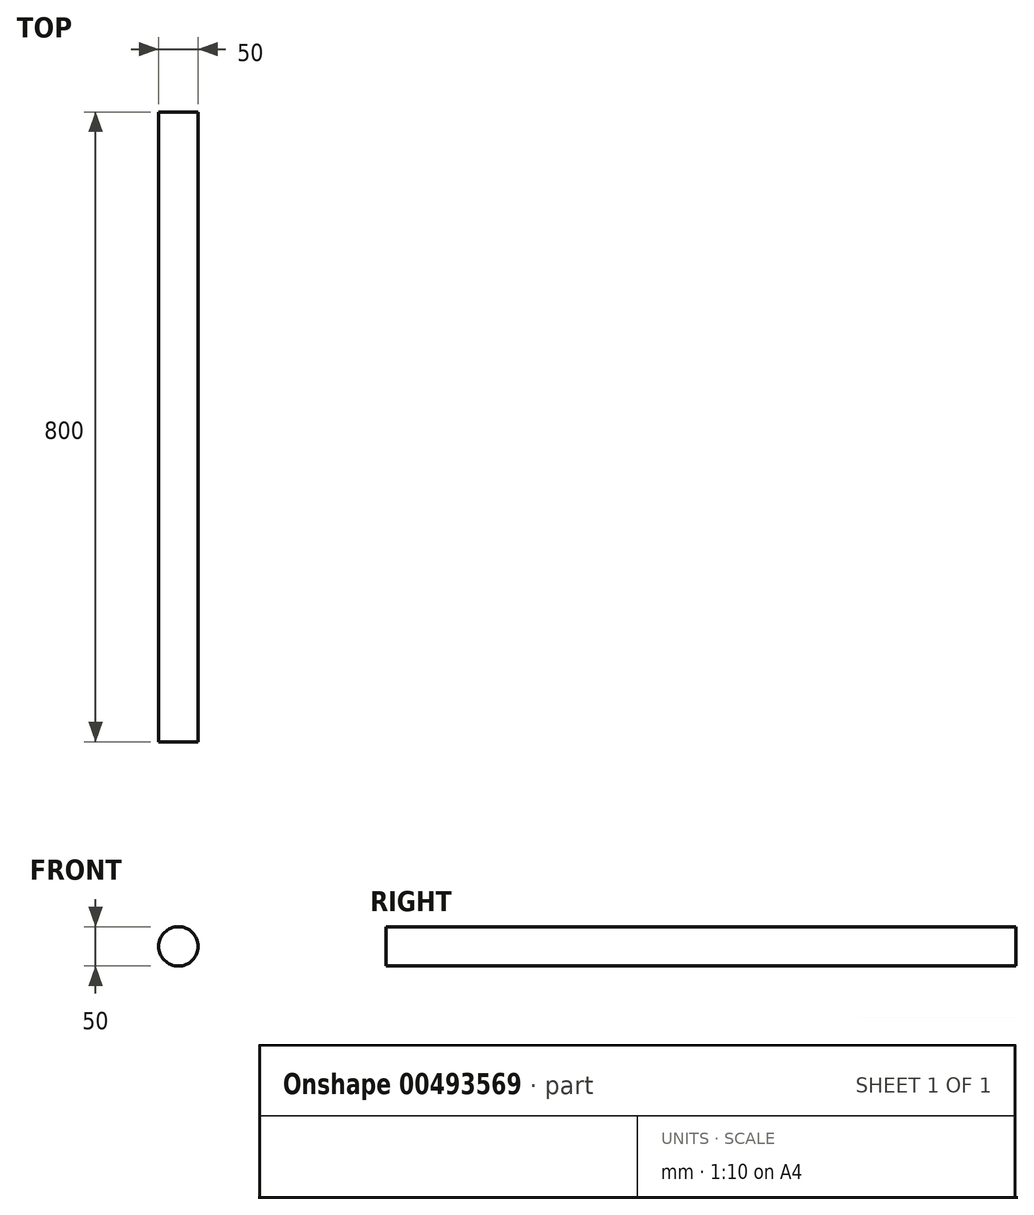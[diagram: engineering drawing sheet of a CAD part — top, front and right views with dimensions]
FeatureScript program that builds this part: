
annotation { "Feature Type Name" : "Feature", "Feature Type Description" : "" }
export const myFeature = defineFeature(function(context is Context, id is Id, definition is map)
    precondition{}
    {
        {
            var Q0;
            Q0=qCreatedBy(makeId("Front.planeOp"),FACE);
            var sketch = newSketch(context, id + "F0", { "sketchPlane" : qUnion([Q0])});
            skCircle(sketch, "E0", {"center": v(0, 0) * mm, "radius": 25 * mm});
            skSolve(sketch);
        }
        {
            var Q0;
            Q0 = qSketchRegion(id + "F0", true);
            extrude(context, id + "F1", {"entities" : qUnion([Q0]), "endBound" : BoundingType.SYMMETRIC, "depth" : 800 * mm});
        }
    });
